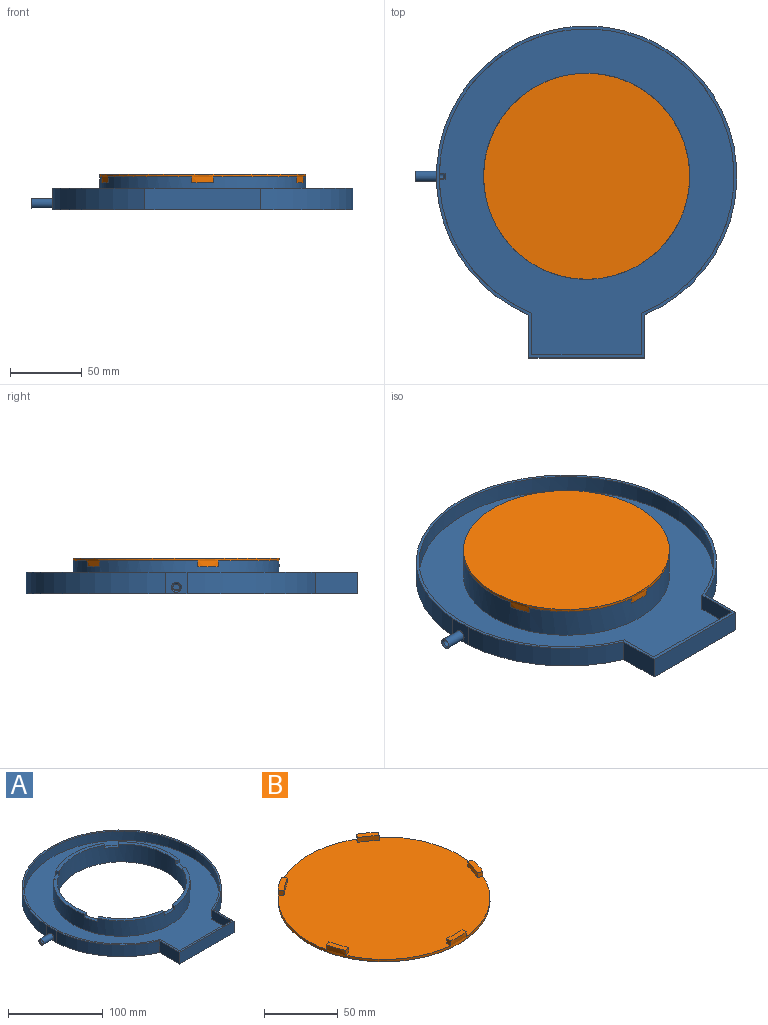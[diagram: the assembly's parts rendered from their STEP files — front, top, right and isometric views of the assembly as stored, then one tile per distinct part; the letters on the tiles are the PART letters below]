
ASSEMBLY  parts=2 mates=1
PART A: 43 faces, bbox 224.7x232x23 mm
  f0: cylinder r=72mm len=144mm, axis (0,0,1), area 8747.2mm2, adj f1,f2,f3,f4,f9,f10,f28,f29
  f1: plane 58.29x43.59mm, normal (0,0,1), area 291.7mm2, adj f0,f7,f37,f41
  f2: plane 68.52x26.21mm, normal (0,0,1), area 291.7mm2, adj f0,f7,f34,f38
  f3: plane 72.05x12.91mm, normal (0,0,1), area 291.7mm2, adj f0,f7,f31,f35
  f4: plane 68.52x26.21mm, normal (0,0,1), area 291.7mm2, adj f0,f7,f28,f32
  f5: cylinder r=105mm len=209.73mm, axis (0,0,-1), area 6689mm2, adj f6,f8,f17,f19
  f6: plane 231.96x209.73mm, normal (0,0,1), area 1444.5mm2, adj f5,f11,f12,f13,f14,f15,f16,f17
  f7: cylinder r=68mm len=136mm, axis (0,0,1), area 9526.3mm2, adj f1,f2,f3,f4,f8,f9,f28,f29
  f8: plane 231.96x209.73mm, normal (0,0,-1), area 22089.1mm2, adj f5,f7,f15,f16,f17,f18,f19
  f9: plane 58.29x43.59mm, normal (0,0,1), area 291.7mm2, adj f0,f7,f29,f40
  f10: plane 227.62x205.98mm, normal (0,0,1), area 18867.3mm2, adj f0,f11,f12,f13,f14,f24,f25,f26
  f11: plane 76.6x12mm, normal (0,1,0), area 919.2mm2, adj f6,f10,f13,f14
  f12: cylinder r=103mm len=206mm, axis (0,0,-1), area 6808.5mm2, adj f6,f10,f13,f14,f20,f24,f26
  f13: plane 29.01x12mm, normal (1,0,0), area 348.1mm2, adj f6,f10,f11,f12
  f14: plane 29.01x12mm, normal (-1,0,0), area 348.1mm2, adj f6,f10,f11,f12
  f15: plane 30x15mm, normal (-1,0,0), area 450mm2, adj f6,f8,f16,f18
  f16: cylinder r=105mm len=89.46mm, axis (0,0,-1), area 1741mm2, adj f6,f8,f15,f19
  f17: plane 30x15mm, normal (1,0,0), area 450mm2, adj f5,f6,f8,f18
  f18: plane 80.6x15mm, normal (0,-1,0), area 1209mm2, adj f6,f8,f15,f17
  f19: plane 15x15mm, normal (-1,0,0), area 186.5mm2, adj f5,f6,f8,f16,f21
  f20: cylinder r=2.4mm len=19.58mm, axis (1,0,0), area 250mm2, adj f12,f23,f24,f25,f26,f27
  f21: cylinder r=3.5mm len=15mm, axis (1,0,0), area 329.9mm2, adj f19,f22
  f22: plane 7x7mm, normal (-1,0,0), area 2.2mm2, adj f21,f27
  f23: plane 1.37x0.1mm, normal (-1,0,0), area 0.1mm2, adj f20,f25
  f24: plane 4.05x0.56mm, normal (0,-0.37,0.93), area 2.4mm2, adj f10,f12,f20,f25
  f25: plane 4.45x0.8mm, normal (-0.71,0,0.71), area 3.3mm2, adj f10,f20,f23,f24,f26
  f26: plane 4.05x0.56mm, normal (0,0.37,0.93), area 2.4mm2, adj f10,f12,f20,f25
  f27: cone r=2.4mm half-angle=45deg, axis (-1,0,0), area 25.8mm2, adj f20,f22
  f28: plane 4x3.83mm, normal (-0.31,-0.95,0), area 16.1mm2, adj f0,f4,f7,f30
  f29: plane 4x3.83mm, normal (0.31,0.95,0), area 16.1mm2, adj f0,f7,f9,f30
  f30: plane 15.51x8.46mm, normal (0,0,1), area 60.1mm2, adj f0,f7,f28,f29
  f31: plane 4x3.26mm, normal (0.81,-0.59,0), area 16.1mm2, adj f0,f3,f7,f33
  f32: plane 4x3.26mm, normal (-0.81,0.59,0), area 16.1mm2, adj f0,f4,f7,f33
  f33: plane 14.5x12.07mm, normal (0,0,1), area 60.1mm2, adj f0,f7,f31,f32
  f34: plane 4x3.26mm, normal (0.81,0.59,0), area 16.1mm2, adj f0,f2,f7,f36
  f35: plane 4x3.26mm, normal (-0.81,-0.59,0), area 16.1mm2, adj f0,f3,f7,f36
  f36: plane 14.5x12.07mm, normal (0,0,1), area 60.1mm2, adj f0,f7,f34,f35
  f37: plane 4x3.83mm, normal (-0.31,0.95,0), area 16.1mm2, adj f0,f1,f7,f39
  f38: plane 4x3.83mm, normal (0.31,-0.95,0), area 16.1mm2, adj f0,f2,f7,f39
  f39: plane 15.51x8.46mm, normal (0,0,1), area 60.1mm2, adj f0,f7,f37,f38
  f40: plane 4.02x4mm, normal (-1,0,0), area 16.1mm2, adj f0,f7,f9,f42
  f41: plane 4.02x4mm, normal (1,0,0), area 16.1mm2, adj f0,f1,f7,f42
  f42: plane 15x4.42mm, normal (0,0,1), area 60.1mm2, adj f0,f7,f40,f41
PART B: 23 faces, bbox 144x144x6 mm
  f0: cylinder r=72mm len=144mm, axis (0,0,-1), area 1205.3mm2, adj f1,f2,f3,f4,f6,f7,f8,f10
  f1: plane 144x143.61mm, normal (0,0,1), area 15985.4mm2, adj f0,f3,f4,f5,f7,f8,f9,f11
  f2: plane 144x144mm, normal (0,0,-1), area 16286mm2, adj f0
  f3: plane 4.02x4mm, normal (-1,0,0), area 16.1mm2, adj f0,f1,f5,f6
  f4: plane 4.02x4mm, normal (1,0,0), area 16.1mm2, adj f0,f1,f5,f6
  f5: cylinder r=68mm len=15mm, axis (0,0,-1), area 60.1mm2, adj f1,f3,f4,f6
  f6: plane 15x4.42mm, normal (0,0,1), area 60.1mm2, adj f0,f3,f4,f5
  f7: plane 4x3.26mm, normal (0.81,-0.59,0), area 16.1mm2, adj f0,f1,f9,f10
  f8: plane 4x3.26mm, normal (-0.81,0.59,0), area 16.1mm2, adj f0,f1,f9,f10
  f9: cylinder r=68mm len=12.14mm, axis (0,0,-1), area 60.1mm2, adj f1,f7,f8,f10
  f10: plane 14.5x12.07mm, normal (0,0,1), area 60.1mm2, adj f0,f7,f8,f9
  f11: plane 4x3.83mm, normal (-0.31,0.95,0), area 16.1mm2, adj f0,f1,f13,f14
  f12: plane 4x3.83mm, normal (0.31,-0.95,0), area 16.1mm2, adj f0,f1,f13,f14
  f13: cylinder r=68mm len=14.27mm, axis (0,0,-1), area 60.1mm2, adj f1,f11,f12,f14
  f14: plane 15.51x8.46mm, normal (0,0,1), area 60.1mm2, adj f0,f11,f12,f13
  f15: plane 4x3.26mm, normal (0.81,0.59,0), area 16.1mm2, adj f0,f1,f17,f18
  f16: plane 4x3.26mm, normal (-0.81,-0.59,0), area 16.1mm2, adj f0,f1,f17,f18
  f17: cylinder r=68mm len=12.14mm, axis (0,0,-1), area 60.1mm2, adj f1,f15,f16,f18
  f18: plane 14.5x12.07mm, normal (0,0,1), area 60.1mm2, adj f0,f15,f16,f17
  f19: plane 4x3.83mm, normal (-0.31,-0.95,0), area 16.1mm2, adj f0,f1,f21,f22
  f20: plane 4x3.83mm, normal (0.31,0.95,0), area 16.1mm2, adj f0,f1,f21,f22
  f21: cylinder r=68mm len=14.27mm, axis (0,0,-1), area 60.1mm2, adj f1,f19,f20,f22
  f22: plane 15.51x8.46mm, normal (0,0,1), area 60.1mm2, adj f0,f19,f20,f21
PLACE A t=(-36.61,-18.01,6.1)mm
PLACE B rot(axis=(-0.95,0.31,0),180deg) t=(125.19,-135.57,8.1)mm
MATE fastened B.f4 <-> A.f32  axis (0.81,-0.59,0) through (10.36,33.88,4.1)mm
